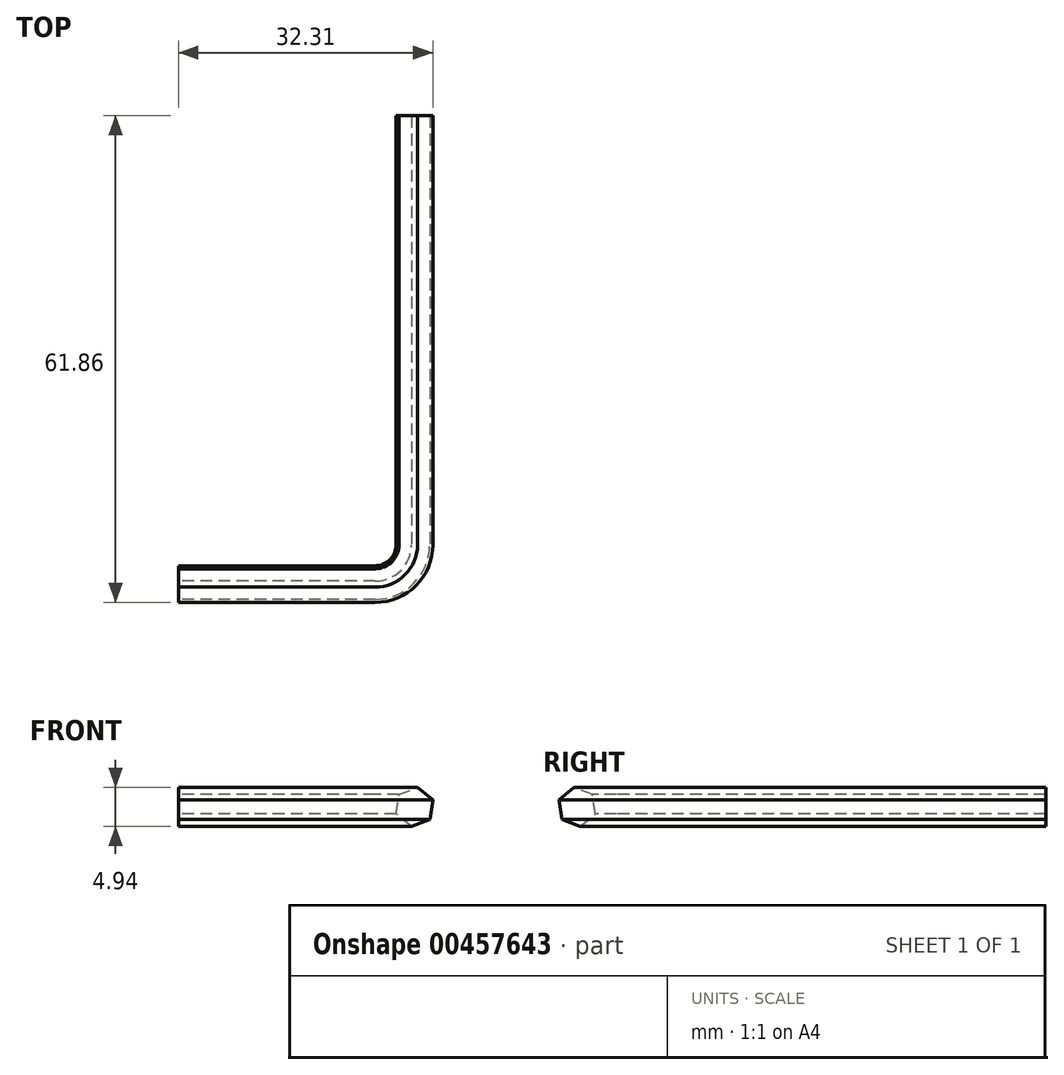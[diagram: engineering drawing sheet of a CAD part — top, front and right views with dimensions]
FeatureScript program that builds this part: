
annotation { "Feature Type Name" : "Feature", "Feature Type Description" : "" }
export const myFeature = defineFeature(function(context is Context, id is Id, definition is map)
    precondition{}
    {
        {
            var Q0;
            Q0=qCreatedBy(makeId("Front.planeOp"),FACE);
            var sketch = newSketch(context, id + "F0", { "sketchPlane" : qUnion([Q0])});
            skCircle(sketch, "E0.cCircle", {"center": v(0, 0) * mm, "radius": 2.17 * mm, "construction": true});
            skLineSegment(sketch, "E0.0", {"start": v(-0.39, -2.47) * mm, "end": v(-2.33, -0.9) * mm});
            skLineSegment(sketch, "E0.1", {"start": v(-2.33, -0.9) * mm, "end": v(-1.95, 1.57) * mm});
            skLineSegment(sketch, "E0.2", {"start": v(-1.95, 1.57) * mm, "end": v(0.39, 2.47) * mm});
            skLineSegment(sketch, "E0.3", {"start": v(0.39, 2.47) * mm, "end": v(2.33, 0.9) * mm});
            skLineSegment(sketch, "E0.4", {"start": v(2.33, 0.9) * mm, "end": v(1.95, -1.57) * mm});
            skLineSegment(sketch, "E0.5", {"start": v(1.95, -1.57) * mm, "end": v(-0.39, -2.47) * mm});
            skPoint(sketch, "E0.0.midPoint", {"position": v(-1.36, -1.69) * mm});
            skSolve(sketch);
        }
        {
            var Q0;
            Q0=qCreatedBy(makeId("Top.planeOp"),FACE);
            var sketch = newSketch(context, id + "F1", { "sketchPlane" : qUnion([Q0])});
            skLineSegment(sketch, "E1", {"start": v(0, 0) * mm, "end": v(0, -54.52) * mm});
            skLineSegment(sketch, "E2", {"start": v(-5, -59.52) * mm, "end": v(-29.98, -59.52) * mm});
            skPoint(sketch, "E3.visualSharp", {"position": v(0, -59.52) * mm});
            skArc(sketch, "E3.filletArc", {"start": v(-5, -59.52) * mm, "mid": v(-1.46, -58.06) * mm, "end": v(0, -54.52) * mm});
            skSolve(sketch);
        }
        {
            var Q0;
            Q0=makeQuery(id+"F0.imprint","IMPRINT",FACE,{"disambiguationData":[TD([[makeQuery(id+"F0.imprint","IMPRINT",EDGE,{"derivedFrom":sQuery(id+"F0.wireOp",EDGE,"E0.0")}),-1.0]])]});
            var Q1;
            Q1=sQuery(id+"F1.wireOp",EDGE,"E1");
            var Q2;
            Q2=sQuery(id+"F1.wireOp",EDGE,"E3.filletArc");
            var Q3;
            Q3=sQuery(id+"F1.wireOp",EDGE,"E2");
            sweep(context, id + "F2", {"profiles" : qUnion([Q0]), "path" : qUnion([Q1, Q2, Q3])});
        }
    });
